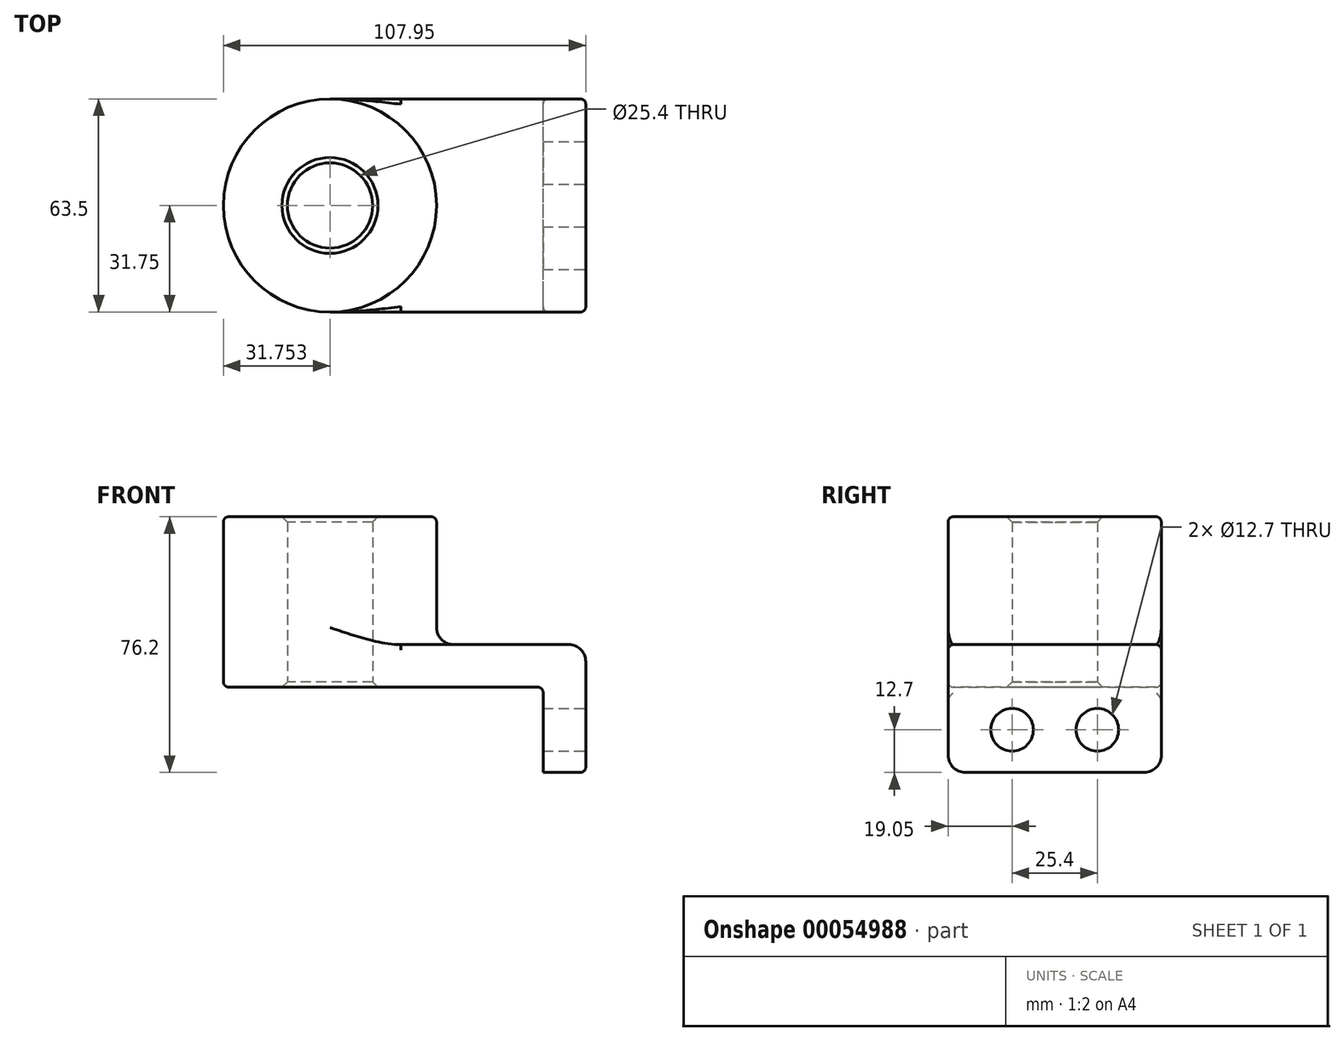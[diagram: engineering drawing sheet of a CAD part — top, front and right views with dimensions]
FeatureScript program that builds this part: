
annotation { "Feature Type Name" : "Feature", "Feature Type Description" : "" }
export const myFeature = defineFeature(function(context is Context, id is Id, definition is map)
    precondition{}
    {
        {
            var Q0;
            Q0=qCreatedBy(makeId("Top.planeOp"),FACE);
            var sketch = newSketch(context, id + "F0", { "sketchPlane" : qUnion([Q0])});
            skLineSegment(sketch, "E0.bottom", {"start": v(-51, 31.75) * mm, "end": v(25.2, 31.75) * mm});
            skLineSegment(sketch, "E0.top", {"start": v(-51, -31.75) * mm, "end": v(25.2, -31.75) * mm});
            skLineSegment(sketch, "E0.left", {"start": v(-51, 31.75) * mm, "end": v(-51, -31.75) * mm});
            skLineSegment(sketch, "E0.right", {"start": v(25.2, 31.75) * mm, "end": v(25.2, -31.75) * mm});
            skCircle(sketch, "E1", {"center": v(-51, 0) * mm, "radius": 31.75 * mm});
            skCircle(sketch, "E2", {"center": v(-51, 0) * mm, "radius": 12.7 * mm});
            skSolve(sketch);
        }
        {
            var Q0;
            Q0 = qSketchRegion(id + "F0", true);
            extrude(context, id + "F1", {"entities" : qUnion([Q0]), "depth" : 12.7 * mm});
        }
        {
            var Q0;
            {var subQ1=sQuery(id+"F0.wireOp",EDGE,"E0.left");var subQ3=sQuery(id+"F0.wireOp",EDGE,"E2");var subQ4=makeQuery(id+"F0.imprint","INTERSECT",VERTEX,{"disambiguationData":[OD(0.0)],"derivedFrom":[subQ1,subQ3]});Q0=makeQuery(id+"F0.imprint","IMPRINT",FACE,{"disambiguationData":[TD([[makeQuery(id+"F0.imprint","IMPRINT",EDGE,{"disambiguationData":[TD([[subQ4,-1.0]])],"derivedFrom":subQ3}),-1.0]])]});}
            var Q1;
            {var subQ1=sQuery(id+"F0.wireOp",EDGE,"E0.left");var subQ3=sQuery(id+"F0.wireOp",EDGE,"E2");var subQ4=makeQuery(id+"F0.imprint","INTERSECT",VERTEX,{"disambiguationData":[OD(0.0)],"derivedFrom":[subQ1,subQ3]});Q1=makeQuery(id+"F0.imprint","IMPRINT",FACE,{"disambiguationData":[TD([[makeQuery(id+"F0.imprint","IMPRINT",EDGE,{"disambiguationData":[TD([[subQ4,1.0]])],"derivedFrom":subQ3}),-1.0]])]});}
            extrude(context, id + "F2", {"entities" : qUnion([Q0, Q1]), "operationType" : NewBodyOperationType.ADD, "depth" : 50.8 * mm});
        }
        {
            var Q0;
            Q0=makeQuery(id+"F1.opExtrude","SWEPT_FACE",FACE,{"disambiguationData":[OSD([sQuery(id+"F0.wireOp",EDGE,"E0.right")])]});
            var sketch = newSketch(context, id + "F3", { "sketchPlane" : qUnion([Q0])});
            skLineSegment(sketch, "E3.bottom", {"start": v(-31.75, 12.7) * mm, "end": v(31.75, 12.7) * mm});
            skLineSegment(sketch, "E3.top", {"start": v(-31.75, -25.4) * mm, "end": v(31.75, -25.4) * mm});
            skLineSegment(sketch, "E3.left", {"start": v(-31.75, 12.7) * mm, "end": v(-31.75, -25.4) * mm});
            skLineSegment(sketch, "E3.right", {"start": v(31.75, 12.7) * mm, "end": v(31.75, -25.4) * mm});
            skCircle(sketch, "E4", {"center": v(-12.7, -12.7) * mm, "radius": 6.35 * mm});
            skLineSegment(sketch, "E5", {"start": v(0, 0) * mm, "end": v(0, -25.4) * mm, "construction": true});
            skCircle(sketch, "E6.MirrorC", {"center": v(12.7, -12.7) * mm, "radius": 6.35 * mm});
            skSolve(sketch);
        }
        {
            var Q0;
            Q0 = qSketchRegion(id + "F3", true);
            extrude(context, id + "F4", {"entities" : qUnion([Q0]), "operationType" : NewBodyOperationType.ADD, "oppositeDirection" : true, "depth" : 12.7 * mm});
        }
        {
            var Q0;
            {var subQ0=sQuery(id+"F0.wireOp",EDGE,"E1");Q0=makeQuery(id+"F2.boolean.opBoolean","INTERSECT",EDGE,{"derivedFrom":[makeQuery(id+"F1.opExtrude","CAP_FACE",FACE,{"disambiguationData":[OSD([sQuery(id+"F0.wireOp",EDGE,"E0.bottom"),sQuery(id+"F0.wireOp",EDGE,"E0.top"),sQuery(id+"F0.wireOp",EDGE,"E0.right"),subQ0,sQuery(id+"F0.wireOp",EDGE,"E2")])],"isStart":false}),makeQuery(id+"F2.opExtrude","SWEPT_FACE",FACE,{"disambiguationData":[OSD([subQ0])]})]});}
            var Q1;
            Q1=makeQuery(id+"F1.opExtrude","CAP_EDGE",EDGE,{"disambiguationData":[OSD([sQuery(id+"F0.wireOp",EDGE,"E0.right")])],"isStart":false});
            var Q2;
            Q2=makeQuery(id+"F4.opExtrude","SWEPT_EDGE",EDGE,{"disambiguationData":[OSD([sQuery(id+"F3.wireOp",EDGE,"E3.top"),sQuery(id+"F3.wireOp",EDGE,"E3.left")])]});
            var Q3;
            Q3=makeQuery(id+"F4.opExtrude","SWEPT_EDGE",EDGE,{"disambiguationData":[OSD([sQuery(id+"F3.wireOp",EDGE,"E3.top"),sQuery(id+"F3.wireOp",EDGE,"E3.right")])]});
            fillet(context, id + "F5", {"entities" : qUnion([Q0, Q1, Q2, Q3]), "radius" : 5.08 * mm, "tangentPropagation" : true, "allowEdgeOverflow" : false});
        }
        {
            var Q0;
            Q0=makeQuery(id+"F1.opExtrude","CAP_EDGE",EDGE,{"disambiguationData":[OSD([sQuery(id+"F0.wireOp",EDGE,"E0.top")])],"isStart":false});
            var Q1;
            Q1=makeQuery(id+"F1.opExtrude","CAP_EDGE",EDGE,{"disambiguationData":[OSD([sQuery(id+"F0.wireOp",EDGE,"E0.bottom")])],"isStart":false});
            var Q2;
            Q2=makeQuery(id+"F1.opExtrude","CAP_EDGE",EDGE,{"disambiguationData":[OSD([sQuery(id+"F0.wireOp",EDGE,"E0.top")])],"isStart":true});
            var Q3;
            Q3=makeQuery(id+"F4.boolean.opBoolean","INTERSECT",EDGE,{"derivedFrom":[makeQuery(id+"F1.opExtrude","CAP_FACE",FACE,{"disambiguationData":[OSD([sQuery(id+"F0.wireOp",EDGE,"E0.bottom"),sQuery(id+"F0.wireOp",EDGE,"E0.top"),sQuery(id+"F0.wireOp",EDGE,"E0.right"),sQuery(id+"F0.wireOp",EDGE,"E1"),sQuery(id+"F0.wireOp",EDGE,"E2")])],"isStart":true}),makeQuery(id+"F4.opExtrude","CAP_FACE",FACE,{"disambiguationData":[OSD([sQuery(id+"F3.wireOp",EDGE,"E3.bottom"),sQuery(id+"F3.wireOp",EDGE,"E3.top"),sQuery(id+"F3.wireOp",EDGE,"E3.left"),sQuery(id+"F3.wireOp",EDGE,"E3.right"),sQuery(id+"F3.wireOp",EDGE,"E4"),sQuery(id+"F3.wireOp",EDGE,"E6.MirrorC")])],"isStart":false})]});
            fillet(context, id + "F6", {"entities" : qUnion([Q0, Q1, Q2, Q3]), "radius" : 1.59 * mm, "tangentPropagation" : true, "allowEdgeOverflow" : false});
        }
        {
            var Q0;
            {var subQ0=sQuery(id+"F0.wireOp",EDGE,"E2");Q0=makeQuery(id+"F2.boolean.opBoolean","MERGE",FACE,{"derivedFrom":[makeQuery(id+"F1.opExtrude","SWEPT_FACE",FACE,{"disambiguationData":[OSD([subQ0])]}),makeQuery(id+"F2.opExtrude","SWEPT_FACE",FACE,{"disambiguationData":[OSD([subQ0])]})]});}
            chamfer(context, id + "F7", {"entities" : qUnion([Q0]), "width" : 1.59 * mm, "tangentPropagation" : true});
        }
        {
            var Q0;
            Q0=makeQuery(id+"F2.opExtrude","CAP_EDGE",EDGE,{"disambiguationData":[OSD([sQuery(id+"F0.wireOp",EDGE,"E1")])],"isStart":false});
            fillet(context, id + "F8", {"entities" : qUnion([Q0]), "radius" : 1.59 * mm, "tangentPropagation" : true, "allowEdgeOverflow" : false});
        }
    });
